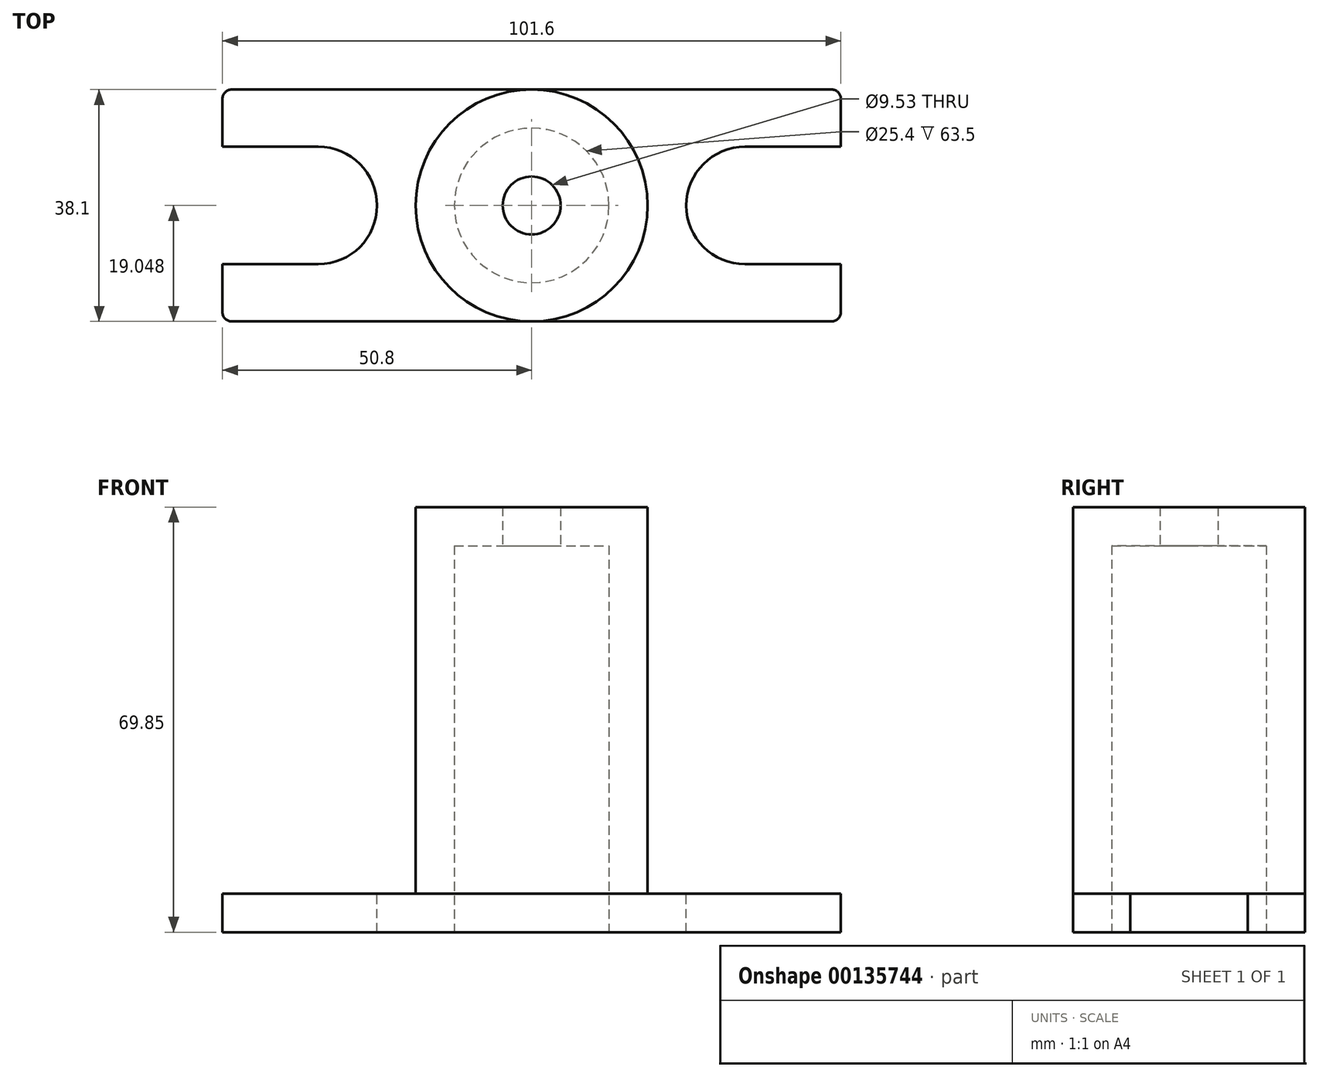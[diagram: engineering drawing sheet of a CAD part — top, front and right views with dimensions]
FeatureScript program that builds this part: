
annotation { "Feature Type Name" : "Feature", "Feature Type Description" : "" }
export const myFeature = defineFeature(function(context is Context, id is Id, definition is map)
    precondition{}
    {
        {
            var Q0;
            Q0=qCreatedBy(makeId("Top.planeOp"),FACE);
            var sketch = newSketch(context, id + "F0", { "sketchPlane" : qUnion([Q0])});
            skLineSegment(sketch, "E0", {"start": v(0, 0) * mm, "end": v(0, 7.87) * mm});
            skLineSegment(sketch, "E1", {"start": v(1.52, 9.4) * mm, "end": v(100.08, 9.4) * mm});
            skLineSegment(sketch, "E2", {"start": v(101.6, 0) * mm, "end": v(85.85, 0) * mm});
            skLineSegment(sketch, "E3", {"start": v(0, 0) * mm, "end": v(15.75, 0) * mm});
            skLineSegment(sketch, "E4", {"start": v(1.52, -28.7) * mm, "end": v(100.08, -28.7) * mm});
            skLineSegment(sketch, "E5", {"start": v(101.6, -27.18) * mm, "end": v(101.6, -19.3) * mm});
            skLineSegment(sketch, "E6", {"start": v(101.6, -19.3) * mm, "end": v(85.85, -19.3) * mm});
            skLineSegment(sketch, "E7", {"start": v(0, -27.18) * mm, "end": v(0, -19.3) * mm});
            skLineSegment(sketch, "E8", {"start": v(0, -19.3) * mm, "end": v(15.75, -19.3) * mm});
            skArc(sketch, "E9", {"start": v(15.75, -19.3) * mm, "mid": v(25.4, -9.65) * mm, "end": v(15.75, 0) * mm});
            skArc(sketch, "E10", {"start": v(85.85, 0) * mm, "mid": v(76.2, -9.65) * mm, "end": v(85.85, -19.3) * mm});
            skPoint(sketch, "E11.visualSharp", {"position": v(0, 9.4) * mm});
            skArc(sketch, "E11.filletArc", {"start": v(1.52, 9.4) * mm, "mid": v(0.45, 8.95) * mm, "end": v(0, 7.87) * mm});
            skPoint(sketch, "E12.visualSharp", {"position": v(101.6, -28.7) * mm});
            skArc(sketch, "E12.filletArc", {"start": v(100.08, -28.7) * mm, "mid": v(101.15, -28.26) * mm, "end": v(101.6, -27.18) * mm});
            skPoint(sketch, "E13.visualSharp", {"position": v(0, -28.7) * mm});
            skArc(sketch, "E13.filletArc", {"start": v(0, -27.18) * mm, "mid": v(0.45, -28.26) * mm, "end": v(1.52, -28.7) * mm});
            skLineSegment(sketch, "E14", {"start": v(101.6, 7.87) * mm, "end": v(101.6, 0) * mm});
            skPoint(sketch, "E15.visualSharp", {"position": v(101.6, 9.4) * mm});
            skArc(sketch, "E15.filletArc", {"start": v(101.6, 7.87) * mm, "mid": v(101.15, 8.95) * mm, "end": v(100.08, 9.4) * mm});
            skPoint(sketch, "E16.centerSnap0", {"position": v(76.2, -9.65) * mm});
            skPoint(sketch, "E16.centerSnap1", {"position": v(50.8, 9.4) * mm});
            skSolve(sketch);
        }
        {
            var Q0;
            Q0=makeQuery(id+"F0.imprint","IMPRINT",FACE,{"disambiguationData":[TD([[makeQuery(id+"F0.imprint","IMPRINT",EDGE,{"derivedFrom":sQuery(id+"F0.wireOp",EDGE,"E0")}),-1.0]])]});
            extrude(context, id + "F1", {"entities" : qUnion([Q0]), "oppositeDirection" : true, "depth" : 6.35 * mm});
        }
        {
            var Q0;
            Q0=makeQuery(id+"F1.opExtrude","CAP_FACE",FACE,{"disambiguationData":[OSD([sQuery(id+"F0.wireOp",EDGE,"E0"),sQuery(id+"F0.wireOp",EDGE,"E1"),sQuery(id+"F0.wireOp",EDGE,"E2"),sQuery(id+"F0.wireOp",EDGE,"E3"),sQuery(id+"F0.wireOp",EDGE,"E4"),sQuery(id+"F0.wireOp",EDGE,"E5"),sQuery(id+"F0.wireOp",EDGE,"E6"),sQuery(id+"F0.wireOp",EDGE,"E7"),sQuery(id+"F0.wireOp",EDGE,"E8"),sQuery(id+"F0.wireOp",EDGE,"E9"),sQuery(id+"F0.wireOp",EDGE,"E10"),sQuery(id+"F0.wireOp",EDGE,"E11.filletArc"),sQuery(id+"F0.wireOp",EDGE,"E12.filletArc"),sQuery(id+"F0.wireOp",EDGE,"E13.filletArc"),sQuery(id+"F0.wireOp",EDGE,"E14"),sQuery(id+"F0.wireOp",EDGE,"E15.filletArc")])],"isStart":true});
            var sketch = newSketch(context, id + "F2", { "sketchPlane" : qUnion([Q0])});
            skCircle(sketch, "E17", {"center": v(50.8, -9.65) * mm, "radius": 19.05 * mm});
            skPoint(sketch, "E17.centerSnap0", {"position": v(50.8, 9.4) * mm});
            skPoint(sketch, "E17.centerSnap1", {"position": v(25.4, -9.65) * mm});
            skCircle(sketch, "E18", {"center": v(50.8, -9.65) * mm, "radius": 4.76 * mm});
            skSolve(sketch);
        }
        {
            var Q0;
            Q0=makeQuery(id+"F2.imprint","IMPRINT",FACE,{"disambiguationData":[TD([[makeQuery(id+"F2.imprint","IMPRINT",EDGE,{"derivedFrom":sQuery(id+"F2.wireOp",EDGE,"E18")}),-1.0]])]});
            extrude(context, id + "F3", {"entities" : qUnion([Q0]), "operationType" : NewBodyOperationType.ADD, "depth" : 63.5 * mm});
        }
        {
            var Q0;
            Q0=makeQuery(id+"F1.opExtrude","CAP_FACE",FACE,{"disambiguationData":[OSD([sQuery(id+"F0.wireOp",EDGE,"E0"),sQuery(id+"F0.wireOp",EDGE,"E1"),sQuery(id+"F0.wireOp",EDGE,"E2"),sQuery(id+"F0.wireOp",EDGE,"E3"),sQuery(id+"F0.wireOp",EDGE,"E4"),sQuery(id+"F0.wireOp",EDGE,"E5"),sQuery(id+"F0.wireOp",EDGE,"E6"),sQuery(id+"F0.wireOp",EDGE,"E7"),sQuery(id+"F0.wireOp",EDGE,"E8"),sQuery(id+"F0.wireOp",EDGE,"E9"),sQuery(id+"F0.wireOp",EDGE,"E10"),sQuery(id+"F0.wireOp",EDGE,"E11.filletArc"),sQuery(id+"F0.wireOp",EDGE,"E12.filletArc"),sQuery(id+"F0.wireOp",EDGE,"E13.filletArc"),sQuery(id+"F0.wireOp",EDGE,"E14"),sQuery(id+"F0.wireOp",EDGE,"E15.filletArc")])],"isStart":false});
            var sketch = newSketch(context, id + "F4", { "sketchPlane" : qUnion([Q0])});
            skCircle(sketch, "E19", {"center": v(50.8, 9.65) * mm, "radius": 12.7 * mm});
            skPoint(sketch, "E19.centerSnap0", {"position": v(25.4, 9.65) * mm});
            skPoint(sketch, "E19.centerSnap1", {"position": v(50.8, -9.4) * mm});
            skSolve(sketch);
        }
        {
            var Q0;
            Q0=makeQuery(id+"F4.imprint","IMPRINT",FACE,{"disambiguationData":[TD([[makeQuery(id+"F4.imprint","IMPRINT",EDGE,{"derivedFrom":sQuery(id+"F4.wireOp",EDGE,"E19")}),1.0]])]});
            extrude(context, id + "F5", {"entities" : qUnion([Q0]), "operationType" : NewBodyOperationType.REMOVE, "oppositeDirection" : true, "depth" : 63.5 * mm});
        }
    });
